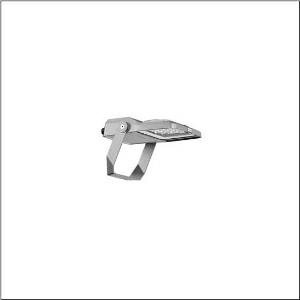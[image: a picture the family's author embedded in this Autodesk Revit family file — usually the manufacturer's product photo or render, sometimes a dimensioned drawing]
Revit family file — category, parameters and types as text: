
# Revit family: floodlight_fl_21_micro___rs12_5xa7762a1b1a_271b
name_source: partatom
category: Lighting Fixtures
units: mm (PartAtom-declared; Revit-internal decimal feet)

## family parameters
Cut with Voids When Loaded = No
Host = Face
Light Source = No
Part Type = Normal
Room Calculation Point = No
Round Connector Dimension = Use Diameter
Shared = No

## types (1)
- --- (1 x LED, 2560 lm, 23.1 W, 2200K)
    Apparent Load = 23 VA
    CIE Flux Codes = 79 92 99 100 100
    Color Rendering = 70
    Color Temperature = 2200K
    Default Elevation = 1800 mm
    Description = Floodlight FL 21 micro, floodlight, primary light control with lens, of PMMA, primary optical cover: protective disc, of toughened safety glass, transparent, light distribution: RS12, light emission: direct distribution, installation type: surface-mounted, LED, High Power LED, rated luminous flux: 2.560lm, luminous efficacy: 111lm/W, light colour: 722, colour temperature: 2200K, control gear: ECG iQ, control: Auto-Match, Temp-Guard, Night-Set, Smart-Wire, Desk-Remote (wireless, voltage-free reading and setting of iQ features in the workshop via application-optimized NFC function/RFID function), optimised constant luminous flux control (CLO 2.0), Street-Remote, with terminal, 6-pole, mains connection: 220..240V, AC, 50/60Hz, start of lifetime: 23W, end of lifetime: 24W, reduction: 11W, luminaire housing, of diecast aluminium, powder-coated, Siteco® metallic grey (DB 702S), corrosivity category C5 according to DIN EN ISO 12944, mounting bracket, of steel, galvanised, powder-coated, Siteco® metallic grey (DB 702S), protection rating (complete): IP66, insulation class (complete): insulation class II (safety insulation), certification: CE, protection symbol: D, impact resistance: IK07, permissible operating ambient temperature: -40..+40°C, permissible operating ambient temperature for outdoor applications: -40..+50°C, standard: DIN EN 12944, packaging unit: 1 piece

Light Distribution: RS12
    Height = 65 mm
    Lamp = 1 x LED
    Lamp Light Flux = 2560 lm
    Lamp Power = 23.1 W
    Lamp count = 1
    Length = 312 mm
    Luminous efficacy = 111 lm/W
    Manufacturer = Siteco
    ModVariant = No
    Model = 5XA7762A1B1A
    Number of Poles = 1
    OnlyDefault = Yes
    Power Factor = 1
    Product Name = Floodlight FL 21 micro | RS12
    Product group = floodlight | pylon top
    ProductGroupID = 6101
    Protection Class = Protection class II
    Protection Degree = IP 66
    RLX_Detail_Level = 1
    RlxData = <blob elided: 74877 chars, md5=776e4d41>
    Socket = socket
    Standby Power = 0 W
    System Light Flux = 2560 lm
    System Power = 23 W
    Type Comments = factory setting: luminous flux: 100 % | dim-lin: 254 | 455 mA
    Type Image = l_1006880.jpg
    URL = http://relux.com
    VarID = @adj_095499
    Voltage = 0 V
    Weight = 0.00 kg
    Width = 230 mm

## geometry (parser evidence)
native form markers: Blend x4, Sweep x13
no freeform markers — native parametric forms only
